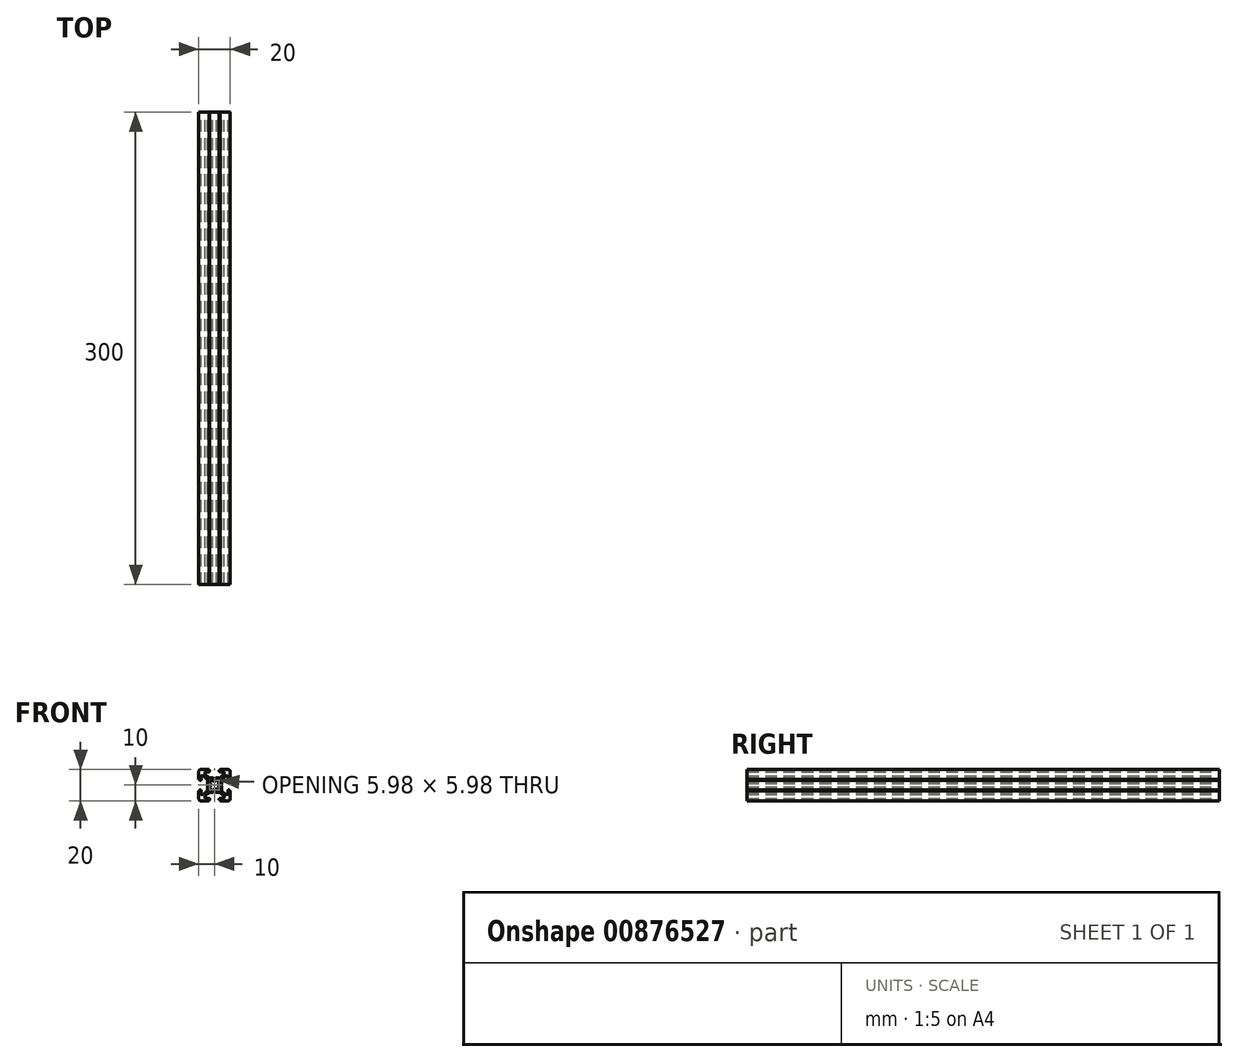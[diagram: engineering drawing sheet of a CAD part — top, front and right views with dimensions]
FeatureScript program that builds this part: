
annotation { "Feature Type Name" : "Feature", "Feature Type Description" : "" }
export const myFeature = defineFeature(function(context is Context, id is Id, definition is map)
    precondition{}
    {
        {
            var Q0;
            Q0=qCreatedBy(makeId("Front.planeOp"),FACE);
            var sketch = newSketch(context, id + "F0", { "sketchPlane" : qUnion([Q0])});
            skLineSegment(sketch, "E0", {"start": v(-222.37, -217.47) * mm, "end": v(-221.83, -218.12) * mm});
            skArc(sketch, "E1", {"start": v(-221.83, -218.12) * mm, "mid": v(-222.13, -219.38) * mm, "end": v(-221.83, -220.64) * mm});
            skLineSegment(sketch, "E2", {"start": v(-221.83, -220.64) * mm, "end": v(-222.37, -221.29) * mm});
            skArc(sketch, "E3", {"start": v(-222.37, -221.29) * mm, "mid": v(-221.9, -221.89) * mm, "end": v(-221.3, -222.37) * mm});
            skLineSegment(sketch, "E4", {"start": v(-221.3, -222.37) * mm, "end": v(-220.64, -221.83) * mm});
            skArc(sketch, "E5", {"start": v(-220.64, -221.83) * mm, "mid": v(-219.38, -222.13) * mm, "end": v(-218.12, -221.83) * mm});
            skLineSegment(sketch, "E6", {"start": v(-218.12, -221.83) * mm, "end": v(-217.47, -222.37) * mm});
            skArc(sketch, "E7", {"start": v(-217.47, -222.37) * mm, "mid": v(-216.87, -221.89) * mm, "end": v(-216.39, -221.29) * mm});
            skLineSegment(sketch, "E8", {"start": v(-216.39, -221.29) * mm, "end": v(-216.93, -220.64) * mm});
            skArc(sketch, "E9", {"start": v(-216.93, -220.64) * mm, "mid": v(-216.63, -219.38) * mm, "end": v(-216.93, -218.12) * mm});
            skLineSegment(sketch, "E10", {"start": v(-216.93, -218.12) * mm, "end": v(-216.39, -217.47) * mm});
            skArc(sketch, "E11", {"start": v(-216.39, -217.47) * mm, "mid": v(-216.87, -216.87) * mm, "end": v(-217.47, -216.4) * mm});
            skLineSegment(sketch, "E12", {"start": v(-217.47, -216.4) * mm, "end": v(-218.12, -216.93) * mm});
            skArc(sketch, "E13", {"start": v(-218.12, -216.93) * mm, "mid": v(-219.38, -216.63) * mm, "end": v(-220.64, -216.93) * mm});
            skLineSegment(sketch, "E14", {"start": v(-220.64, -216.93) * mm, "end": v(-221.3, -216.4) * mm});
            skArc(sketch, "E15", {"start": v(-221.3, -216.4) * mm, "mid": v(-221.9, -216.87) * mm, "end": v(-222.37, -217.47) * mm});
            skLineSegment(sketch, "E16", {"start": v(-223.13, -209.38) * mm, "end": v(-227.88, -209.38) * mm});
            skArc(sketch, "E17", {"start": v(-222.93, -209.58) * mm, "mid": v(-222.99, -209.44) * mm, "end": v(-223.13, -209.38) * mm});
            skLineSegment(sketch, "E18", {"start": v(-222.93, -209.68) * mm, "end": v(-222.93, -209.58) * mm});
            skArc(sketch, "E19", {"start": v(-222.93, -209.68) * mm, "mid": v(-222.87, -209.82) * mm, "end": v(-222.73, -209.88) * mm});
            skLineSegment(sketch, "E20", {"start": v(-222.58, -209.88) * mm, "end": v(-222.73, -209.88) * mm});
            skArc(sketch, "E21", {"start": v(-222.38, -210.08) * mm, "mid": v(-222.44, -209.94) * mm, "end": v(-222.58, -209.88) * mm});
            skLineSegment(sketch, "E22", {"start": v(-222.38, -210.38) * mm, "end": v(-222.38, -210.08) * mm});
            skArc(sketch, "E23", {"start": v(-222.88, -210.88) * mm, "mid": v(-222.53, -210.73) * mm, "end": v(-222.38, -210.38) * mm});
            skLineSegment(sketch, "E24", {"start": v(-224.88, -210.88) * mm, "end": v(-222.88, -210.88) * mm});
            skArc(sketch, "E25", {"start": v(-224.88, -210.88) * mm, "mid": v(-225.23, -211.03) * mm, "end": v(-225.38, -211.38) * mm});
            skLineSegment(sketch, "E26", {"start": v(-225.38, -212.11) * mm, "end": v(-225.38, -211.38) * mm});
            skArc(sketch, "E27", {"start": v(-225.38, -212.11) * mm, "mid": v(-225.34, -212.3) * mm, "end": v(-225.23, -212.47) * mm});
            skLineSegment(sketch, "E28", {"start": v(-222.97, -214.73) * mm, "end": v(-225.23, -212.47) * mm});
            skArc(sketch, "E29", {"start": v(-222.97, -214.73) * mm, "mid": v(-222.8, -214.84) * mm, "end": v(-222.61, -214.88) * mm});
            skLineSegment(sketch, "E30", {"start": v(-220.33, -214.88) * mm, "end": v(-222.61, -214.88) * mm});
            skArc(sketch, "E31", {"start": v(-220.23, -214.9) * mm, "mid": v(-220.28, -214.89) * mm, "end": v(-220.33, -214.88) * mm});
            skLineSegment(sketch, "E32", {"start": v(-219.48, -215.34) * mm, "end": v(-220.23, -214.9) * mm});
            skArc(sketch, "E33", {"start": v(-219.48, -215.34) * mm, "mid": v(-219.38, -215.37) * mm, "end": v(-219.28, -215.34) * mm});
            skLineSegment(sketch, "E34", {"start": v(-218.53, -214.9) * mm, "end": v(-219.28, -215.34) * mm});
            skArc(sketch, "E35", {"start": v(-218.43, -214.88) * mm, "mid": v(-218.48, -214.89) * mm, "end": v(-218.53, -214.9) * mm});
            skLineSegment(sketch, "E36", {"start": v(-216.15, -214.88) * mm, "end": v(-218.43, -214.88) * mm});
            skArc(sketch, "E37", {"start": v(-216.15, -214.88) * mm, "mid": v(-215.96, -214.84) * mm, "end": v(-215.8, -214.73) * mm});
            skLineSegment(sketch, "E38", {"start": v(-213.53, -212.47) * mm, "end": v(-215.8, -214.73) * mm});
            skArc(sketch, "E39", {"start": v(-213.53, -212.47) * mm, "mid": v(-213.42, -212.3) * mm, "end": v(-213.38, -212.11) * mm});
            skLineSegment(sketch, "E40", {"start": v(-213.38, -211.38) * mm, "end": v(-213.38, -212.11) * mm});
            skArc(sketch, "E41", {"start": v(-213.38, -211.38) * mm, "mid": v(-213.53, -211.03) * mm, "end": v(-213.88, -210.88) * mm});
            skLineSegment(sketch, "E42", {"start": v(-215.88, -210.88) * mm, "end": v(-213.88, -210.88) * mm});
            skArc(sketch, "E43", {"start": v(-216.38, -210.38) * mm, "mid": v(-216.23, -210.73) * mm, "end": v(-215.88, -210.88) * mm});
            skLineSegment(sketch, "E44", {"start": v(-216.38, -210.08) * mm, "end": v(-216.38, -210.38) * mm});
            skArc(sketch, "E45", {"start": v(-216.18, -209.88) * mm, "mid": v(-216.32, -209.94) * mm, "end": v(-216.38, -210.08) * mm});
            skLineSegment(sketch, "E46", {"start": v(-216.03, -209.88) * mm, "end": v(-216.18, -209.88) * mm});
            skArc(sketch, "E47", {"start": v(-216.03, -209.88) * mm, "mid": v(-215.89, -209.82) * mm, "end": v(-215.83, -209.68) * mm});
            skLineSegment(sketch, "E48", {"start": v(-215.83, -209.58) * mm, "end": v(-215.83, -209.68) * mm});
            skArc(sketch, "E49", {"start": v(-215.63, -209.38) * mm, "mid": v(-215.77, -209.44) * mm, "end": v(-215.83, -209.58) * mm});
            skLineSegment(sketch, "E50", {"start": v(-210.88, -209.38) * mm, "end": v(-215.63, -209.38) * mm});
            skArc(sketch, "E51", {"start": v(-209.38, -210.88) * mm, "mid": v(-209.82, -209.82) * mm, "end": v(-210.88, -209.38) * mm});
            skLineSegment(sketch, "E52", {"start": v(-209.38, -215.63) * mm, "end": v(-209.38, -210.88) * mm});
            skArc(sketch, "E53", {"start": v(-209.58, -215.83) * mm, "mid": v(-209.44, -215.77) * mm, "end": v(-209.38, -215.63) * mm});
            skLineSegment(sketch, "E54", {"start": v(-209.68, -215.83) * mm, "end": v(-209.58, -215.83) * mm});
            skArc(sketch, "E55", {"start": v(-209.68, -215.83) * mm, "mid": v(-209.82, -215.89) * mm, "end": v(-209.88, -216.03) * mm});
            skLineSegment(sketch, "E56", {"start": v(-209.88, -216.18) * mm, "end": v(-209.88, -216.03) * mm});
            skArc(sketch, "E57", {"start": v(-210.08, -216.38) * mm, "mid": v(-209.94, -216.32) * mm, "end": v(-209.88, -216.18) * mm});
            skLineSegment(sketch, "E58", {"start": v(-210.38, -216.38) * mm, "end": v(-210.08, -216.38) * mm});
            skArc(sketch, "E59", {"start": v(-210.88, -215.88) * mm, "mid": v(-210.73, -216.23) * mm, "end": v(-210.38, -216.38) * mm});
            skLineSegment(sketch, "E60", {"start": v(-210.88, -213.88) * mm, "end": v(-210.88, -215.88) * mm});
            skArc(sketch, "E61", {"start": v(-210.88, -213.88) * mm, "mid": v(-211.03, -213.53) * mm, "end": v(-211.38, -213.38) * mm});
            skLineSegment(sketch, "E62", {"start": v(-212.11, -213.38) * mm, "end": v(-211.38, -213.38) * mm});
            skArc(sketch, "E63", {"start": v(-212.11, -213.38) * mm, "mid": v(-212.3, -213.42) * mm, "end": v(-212.47, -213.53) * mm});
            skLineSegment(sketch, "E64", {"start": v(-214.73, -215.8) * mm, "end": v(-212.47, -213.53) * mm});
            skArc(sketch, "E65", {"start": v(-214.73, -215.8) * mm, "mid": v(-214.84, -215.96) * mm, "end": v(-214.88, -216.15) * mm});
            skLineSegment(sketch, "E66", {"start": v(-214.88, -218.43) * mm, "end": v(-214.88, -216.15) * mm});
            skArc(sketch, "E67", {"start": v(-214.9, -218.53) * mm, "mid": v(-214.89, -218.48) * mm, "end": v(-214.88, -218.43) * mm});
            skLineSegment(sketch, "E68", {"start": v(-215.34, -219.28) * mm, "end": v(-214.9, -218.53) * mm});
            skArc(sketch, "E69", {"start": v(-215.34, -219.28) * mm, "mid": v(-215.37, -219.38) * mm, "end": v(-215.34, -219.48) * mm});
            skLineSegment(sketch, "E70", {"start": v(-214.9, -220.23) * mm, "end": v(-215.34, -219.48) * mm});
            skArc(sketch, "E71", {"start": v(-214.88, -220.33) * mm, "mid": v(-214.89, -220.28) * mm, "end": v(-214.9, -220.23) * mm});
            skLineSegment(sketch, "E72", {"start": v(-214.88, -222.61) * mm, "end": v(-214.88, -220.33) * mm});
            skArc(sketch, "E73", {"start": v(-214.88, -222.61) * mm, "mid": v(-214.84, -222.8) * mm, "end": v(-214.73, -222.97) * mm});
            skLineSegment(sketch, "E74", {"start": v(-212.47, -225.23) * mm, "end": v(-214.73, -222.97) * mm});
            skArc(sketch, "E75", {"start": v(-212.47, -225.23) * mm, "mid": v(-212.3, -225.34) * mm, "end": v(-212.11, -225.38) * mm});
            skLineSegment(sketch, "E76", {"start": v(-211.38, -225.38) * mm, "end": v(-212.11, -225.38) * mm});
            skArc(sketch, "E77", {"start": v(-211.38, -225.38) * mm, "mid": v(-211.03, -225.23) * mm, "end": v(-210.88, -224.88) * mm});
            skLineSegment(sketch, "E78", {"start": v(-210.88, -222.88) * mm, "end": v(-210.88, -224.88) * mm});
            skArc(sketch, "E79", {"start": v(-210.38, -222.38) * mm, "mid": v(-210.73, -222.53) * mm, "end": v(-210.88, -222.88) * mm});
            skLineSegment(sketch, "E80", {"start": v(-210.08, -222.38) * mm, "end": v(-210.38, -222.38) * mm});
            skArc(sketch, "E81", {"start": v(-209.88, -222.58) * mm, "mid": v(-209.94, -222.44) * mm, "end": v(-210.08, -222.38) * mm});
            skLineSegment(sketch, "E82", {"start": v(-209.88, -222.73) * mm, "end": v(-209.88, -222.58) * mm});
            skArc(sketch, "E83", {"start": v(-209.88, -222.73) * mm, "mid": v(-209.82, -222.87) * mm, "end": v(-209.68, -222.93) * mm});
            skLineSegment(sketch, "E84", {"start": v(-209.58, -222.93) * mm, "end": v(-209.68, -222.93) * mm});
            skArc(sketch, "E85", {"start": v(-209.38, -223.13) * mm, "mid": v(-209.44, -222.99) * mm, "end": v(-209.58, -222.93) * mm});
            skLineSegment(sketch, "E86", {"start": v(-209.38, -227.88) * mm, "end": v(-209.38, -223.13) * mm});
            skArc(sketch, "E87", {"start": v(-210.88, -229.38) * mm, "mid": v(-209.82, -228.94) * mm, "end": v(-209.38, -227.88) * mm});
            skLineSegment(sketch, "E88", {"start": v(-215.63, -229.38) * mm, "end": v(-210.88, -229.38) * mm});
            skArc(sketch, "E89", {"start": v(-215.83, -229.18) * mm, "mid": v(-215.77, -229.32) * mm, "end": v(-215.63, -229.38) * mm});
            skLineSegment(sketch, "E90", {"start": v(-215.83, -229.08) * mm, "end": v(-215.83, -229.18) * mm});
            skArc(sketch, "E91", {"start": v(-215.83, -229.08) * mm, "mid": v(-215.89, -228.94) * mm, "end": v(-216.03, -228.88) * mm});
            skLineSegment(sketch, "E92", {"start": v(-216.18, -228.88) * mm, "end": v(-216.03, -228.88) * mm});
            skArc(sketch, "E93", {"start": v(-216.38, -228.68) * mm, "mid": v(-216.32, -228.82) * mm, "end": v(-216.18, -228.88) * mm});
            skLineSegment(sketch, "E94", {"start": v(-216.38, -228.38) * mm, "end": v(-216.38, -228.68) * mm});
            skArc(sketch, "E95", {"start": v(-215.88, -227.88) * mm, "mid": v(-216.23, -228.03) * mm, "end": v(-216.38, -228.38) * mm});
            skLineSegment(sketch, "E96", {"start": v(-213.88, -227.88) * mm, "end": v(-215.88, -227.88) * mm});
            skArc(sketch, "E97", {"start": v(-213.88, -227.88) * mm, "mid": v(-213.53, -227.73) * mm, "end": v(-213.38, -227.38) * mm});
            skLineSegment(sketch, "E98", {"start": v(-213.38, -226.65) * mm, "end": v(-213.38, -227.38) * mm});
            skArc(sketch, "E99", {"start": v(-213.38, -226.65) * mm, "mid": v(-213.42, -226.46) * mm, "end": v(-213.53, -226.3) * mm});
            skLineSegment(sketch, "E100", {"start": v(-215.8, -224.03) * mm, "end": v(-213.53, -226.3) * mm});
            skArc(sketch, "E101", {"start": v(-215.8, -224.03) * mm, "mid": v(-215.96, -223.92) * mm, "end": v(-216.15, -223.88) * mm});
            skLineSegment(sketch, "E102", {"start": v(-218.43, -223.88) * mm, "end": v(-216.15, -223.88) * mm});
            skArc(sketch, "E103", {"start": v(-218.53, -223.85) * mm, "mid": v(-218.48, -223.87) * mm, "end": v(-218.43, -223.88) * mm});
            skLineSegment(sketch, "E104", {"start": v(-219.28, -223.42) * mm, "end": v(-218.53, -223.85) * mm});
            skArc(sketch, "E105", {"start": v(-219.28, -223.42) * mm, "mid": v(-219.38, -223.4) * mm, "end": v(-219.48, -223.42) * mm});
            skLineSegment(sketch, "E106", {"start": v(-220.23, -223.85) * mm, "end": v(-219.48, -223.42) * mm});
            skArc(sketch, "E107", {"start": v(-220.33, -223.88) * mm, "mid": v(-220.28, -223.87) * mm, "end": v(-220.23, -223.85) * mm});
            skLineSegment(sketch, "E108", {"start": v(-222.61, -223.88) * mm, "end": v(-220.33, -223.88) * mm});
            skArc(sketch, "E109", {"start": v(-222.61, -223.88) * mm, "mid": v(-222.8, -223.92) * mm, "end": v(-222.97, -224.03) * mm});
            skLineSegment(sketch, "E110", {"start": v(-225.23, -226.3) * mm, "end": v(-222.97, -224.03) * mm});
            skArc(sketch, "E111", {"start": v(-225.23, -226.3) * mm, "mid": v(-225.34, -226.46) * mm, "end": v(-225.38, -226.65) * mm});
            skLineSegment(sketch, "E112", {"start": v(-225.38, -227.38) * mm, "end": v(-225.38, -226.65) * mm});
            skArc(sketch, "E113", {"start": v(-225.38, -227.38) * mm, "mid": v(-225.23, -227.73) * mm, "end": v(-224.88, -227.88) * mm});
            skLineSegment(sketch, "E114", {"start": v(-222.88, -227.88) * mm, "end": v(-224.88, -227.88) * mm});
            skArc(sketch, "E115", {"start": v(-222.38, -228.38) * mm, "mid": v(-222.53, -228.03) * mm, "end": v(-222.88, -227.88) * mm});
            skLineSegment(sketch, "E116", {"start": v(-222.38, -228.68) * mm, "end": v(-222.38, -228.38) * mm});
            skArc(sketch, "E117", {"start": v(-222.58, -228.88) * mm, "mid": v(-222.44, -228.82) * mm, "end": v(-222.38, -228.68) * mm});
            skLineSegment(sketch, "E118", {"start": v(-222.73, -228.88) * mm, "end": v(-222.58, -228.88) * mm});
            skArc(sketch, "E119", {"start": v(-222.73, -228.88) * mm, "mid": v(-222.87, -228.94) * mm, "end": v(-222.93, -229.08) * mm});
            skLineSegment(sketch, "E120", {"start": v(-222.93, -229.18) * mm, "end": v(-222.93, -229.08) * mm});
            skArc(sketch, "E121", {"start": v(-223.13, -229.38) * mm, "mid": v(-222.99, -229.32) * mm, "end": v(-222.93, -229.18) * mm});
            skLineSegment(sketch, "E122", {"start": v(-227.88, -229.38) * mm, "end": v(-223.13, -229.38) * mm});
            skArc(sketch, "E123", {"start": v(-229.38, -227.88) * mm, "mid": v(-228.94, -228.94) * mm, "end": v(-227.88, -229.38) * mm});
            skLineSegment(sketch, "E124", {"start": v(-229.38, -223.13) * mm, "end": v(-229.38, -227.88) * mm});
            skArc(sketch, "E125", {"start": v(-229.18, -222.93) * mm, "mid": v(-229.32, -222.99) * mm, "end": v(-229.38, -223.13) * mm});
            skLineSegment(sketch, "E126", {"start": v(-229.08, -222.93) * mm, "end": v(-229.18, -222.93) * mm});
            skArc(sketch, "E127", {"start": v(-229.08, -222.93) * mm, "mid": v(-228.94, -222.87) * mm, "end": v(-228.88, -222.73) * mm});
            skLineSegment(sketch, "E128", {"start": v(-228.88, -222.58) * mm, "end": v(-228.88, -222.73) * mm});
            skArc(sketch, "E129", {"start": v(-228.68, -222.38) * mm, "mid": v(-228.82, -222.44) * mm, "end": v(-228.88, -222.58) * mm});
            skLineSegment(sketch, "E130", {"start": v(-228.38, -222.38) * mm, "end": v(-228.68, -222.38) * mm});
            skArc(sketch, "E131", {"start": v(-227.88, -222.88) * mm, "mid": v(-228.03, -222.53) * mm, "end": v(-228.38, -222.38) * mm});
            skLineSegment(sketch, "E132", {"start": v(-227.88, -224.88) * mm, "end": v(-227.88, -222.88) * mm});
            skArc(sketch, "E133", {"start": v(-227.88, -224.88) * mm, "mid": v(-227.73, -225.23) * mm, "end": v(-227.38, -225.38) * mm});
            skLineSegment(sketch, "E134", {"start": v(-226.65, -225.38) * mm, "end": v(-227.38, -225.38) * mm});
            skArc(sketch, "E135", {"start": v(-226.65, -225.38) * mm, "mid": v(-226.46, -225.34) * mm, "end": v(-226.3, -225.23) * mm});
            skLineSegment(sketch, "E136", {"start": v(-224.03, -222.97) * mm, "end": v(-226.3, -225.23) * mm});
            skArc(sketch, "E137", {"start": v(-224.03, -222.97) * mm, "mid": v(-223.92, -222.8) * mm, "end": v(-223.88, -222.61) * mm});
            skLineSegment(sketch, "E138", {"start": v(-223.88, -220.33) * mm, "end": v(-223.88, -222.61) * mm});
            skArc(sketch, "E139", {"start": v(-223.85, -220.23) * mm, "mid": v(-223.87, -220.28) * mm, "end": v(-223.88, -220.33) * mm});
            skLineSegment(sketch, "E140", {"start": v(-223.42, -219.48) * mm, "end": v(-223.85, -220.23) * mm});
            skArc(sketch, "E141", {"start": v(-223.42, -219.48) * mm, "mid": v(-223.4, -219.38) * mm, "end": v(-223.42, -219.28) * mm});
            skLineSegment(sketch, "E142", {"start": v(-223.85, -218.53) * mm, "end": v(-223.42, -219.28) * mm});
            skArc(sketch, "E143", {"start": v(-223.88, -218.43) * mm, "mid": v(-223.87, -218.48) * mm, "end": v(-223.85, -218.53) * mm});
            skLineSegment(sketch, "E144", {"start": v(-223.88, -216.15) * mm, "end": v(-223.88, -218.43) * mm});
            skArc(sketch, "E145", {"start": v(-223.88, -216.15) * mm, "mid": v(-223.92, -215.96) * mm, "end": v(-224.03, -215.8) * mm});
            skLineSegment(sketch, "E146", {"start": v(-226.3, -213.53) * mm, "end": v(-224.03, -215.8) * mm});
            skArc(sketch, "E147", {"start": v(-226.3, -213.53) * mm, "mid": v(-226.46, -213.42) * mm, "end": v(-226.65, -213.38) * mm});
            skLineSegment(sketch, "E148", {"start": v(-227.38, -213.38) * mm, "end": v(-226.65, -213.38) * mm});
            skArc(sketch, "E149", {"start": v(-227.38, -213.38) * mm, "mid": v(-227.73, -213.53) * mm, "end": v(-227.88, -213.88) * mm});
            skLineSegment(sketch, "E150", {"start": v(-227.88, -215.88) * mm, "end": v(-227.88, -213.88) * mm});
            skArc(sketch, "E151", {"start": v(-228.38, -216.38) * mm, "mid": v(-228.03, -216.23) * mm, "end": v(-227.88, -215.88) * mm});
            skLineSegment(sketch, "E152", {"start": v(-228.68, -216.38) * mm, "end": v(-228.38, -216.38) * mm});
            skArc(sketch, "E153", {"start": v(-228.88, -216.18) * mm, "mid": v(-228.82, -216.32) * mm, "end": v(-228.68, -216.38) * mm});
            skLineSegment(sketch, "E154", {"start": v(-228.88, -216.03) * mm, "end": v(-228.88, -216.18) * mm});
            skArc(sketch, "E155", {"start": v(-228.88, -216.03) * mm, "mid": v(-228.94, -215.89) * mm, "end": v(-229.08, -215.83) * mm});
            skLineSegment(sketch, "E156", {"start": v(-229.18, -215.83) * mm, "end": v(-229.08, -215.83) * mm});
            skArc(sketch, "E157", {"start": v(-229.38, -215.63) * mm, "mid": v(-229.32, -215.77) * mm, "end": v(-229.18, -215.83) * mm});
            skLineSegment(sketch, "E158", {"start": v(-229.38, -210.88) * mm, "end": v(-229.38, -215.63) * mm});
            skArc(sketch, "E159", {"start": v(-227.88, -209.38) * mm, "mid": v(-228.94, -209.82) * mm, "end": v(-229.38, -210.88) * mm});
            skSolve(sketch);
        }
        {
            var Q0;
            Q0=makeQuery(id+"F0.imprint","IMPRINT",FACE,{"disambiguationData":[TD([[makeQuery(id+"F0.imprint","IMPRINT",EDGE,{"derivedFrom":sQuery(id+"F0.wireOp",EDGE,"E0")}),-1.0]])]});
            extrude(context, id + "F1", {"entities" : qUnion([Q0]), "depth" : 300 * mm, "offsetDistance" : 25 * mm});
        }
        {
            var Q0;
            Q0=makeQuery(id+"F1.opExtrude","CAP_FACE",FACE,{"disambiguationData":[OSD([sQuery(id+"F0.wireOp",EDGE,"E0"),sQuery(id+"F0.wireOp",EDGE,"E1"),sQuery(id+"F0.wireOp",EDGE,"E2"),sQuery(id+"F0.wireOp",EDGE,"E3"),sQuery(id+"F0.wireOp",EDGE,"E4"),sQuery(id+"F0.wireOp",EDGE,"E5"),sQuery(id+"F0.wireOp",EDGE,"E6"),sQuery(id+"F0.wireOp",EDGE,"E7"),sQuery(id+"F0.wireOp",EDGE,"E8"),sQuery(id+"F0.wireOp",EDGE,"E9"),sQuery(id+"F0.wireOp",EDGE,"E10"),sQuery(id+"F0.wireOp",EDGE,"E11"),sQuery(id+"F0.wireOp",EDGE,"E12"),sQuery(id+"F0.wireOp",EDGE,"E13"),sQuery(id+"F0.wireOp",EDGE,"E14"),sQuery(id+"F0.wireOp",EDGE,"E15"),sQuery(id+"F0.wireOp",EDGE,"E16"),sQuery(id+"F0.wireOp",EDGE,"E17"),sQuery(id+"F0.wireOp",EDGE,"E18"),sQuery(id+"F0.wireOp",EDGE,"E19"),sQuery(id+"F0.wireOp",EDGE,"E20"),sQuery(id+"F0.wireOp",EDGE,"E21"),sQuery(id+"F0.wireOp",EDGE,"E22"),sQuery(id+"F0.wireOp",EDGE,"E23"),sQuery(id+"F0.wireOp",EDGE,"E24"),sQuery(id+"F0.wireOp",EDGE,"E25"),sQuery(id+"F0.wireOp",EDGE,"E26"),sQuery(id+"F0.wireOp",EDGE,"E27"),sQuery(id+"F0.wireOp",EDGE,"E28"),sQuery(id+"F0.wireOp",EDGE,"E29"),sQuery(id+"F0.wireOp",EDGE,"E30"),sQuery(id+"F0.wireOp",EDGE,"E31"),sQuery(id+"F0.wireOp",EDGE,"E32"),sQuery(id+"F0.wireOp",EDGE,"E33"),sQuery(id+"F0.wireOp",EDGE,"E34"),sQuery(id+"F0.wireOp",EDGE,"E35"),sQuery(id+"F0.wireOp",EDGE,"E36"),sQuery(id+"F0.wireOp",EDGE,"E37"),sQuery(id+"F0.wireOp",EDGE,"E38"),sQuery(id+"F0.wireOp",EDGE,"E39"),sQuery(id+"F0.wireOp",EDGE,"E40"),sQuery(id+"F0.wireOp",EDGE,"E41"),sQuery(id+"F0.wireOp",EDGE,"E42"),sQuery(id+"F0.wireOp",EDGE,"E43"),sQuery(id+"F0.wireOp",EDGE,"E44"),sQuery(id+"F0.wireOp",EDGE,"E45"),sQuery(id+"F0.wireOp",EDGE,"E46"),sQuery(id+"F0.wireOp",EDGE,"E47"),sQuery(id+"F0.wireOp",EDGE,"E48"),sQuery(id+"F0.wireOp",EDGE,"E49"),sQuery(id+"F0.wireOp",EDGE,"E50"),sQuery(id+"F0.wireOp",EDGE,"E51"),sQuery(id+"F0.wireOp",EDGE,"E52"),sQuery(id+"F0.wireOp",EDGE,"E53"),sQuery(id+"F0.wireOp",EDGE,"E54"),sQuery(id+"F0.wireOp",EDGE,"E55"),sQuery(id+"F0.wireOp",EDGE,"E56"),sQuery(id+"F0.wireOp",EDGE,"E57"),sQuery(id+"F0.wireOp",EDGE,"E58"),sQuery(id+"F0.wireOp",EDGE,"E59"),sQuery(id+"F0.wireOp",EDGE,"E60"),sQuery(id+"F0.wireOp",EDGE,"E61"),sQuery(id+"F0.wireOp",EDGE,"E62"),sQuery(id+"F0.wireOp",EDGE,"E63"),sQuery(id+"F0.wireOp",EDGE,"E64"),sQuery(id+"F0.wireOp",EDGE,"E65"),sQuery(id+"F0.wireOp",EDGE,"E66"),sQuery(id+"F0.wireOp",EDGE,"E67"),sQuery(id+"F0.wireOp",EDGE,"E68"),sQuery(id+"F0.wireOp",EDGE,"E69"),sQuery(id+"F0.wireOp",EDGE,"E70"),sQuery(id+"F0.wireOp",EDGE,"E71"),sQuery(id+"F0.wireOp",EDGE,"E72"),sQuery(id+"F0.wireOp",EDGE,"E73"),sQuery(id+"F0.wireOp",EDGE,"E74"),sQuery(id+"F0.wireOp",EDGE,"E75"),sQuery(id+"F0.wireOp",EDGE,"E76"),sQuery(id+"F0.wireOp",EDGE,"E77"),sQuery(id+"F0.wireOp",EDGE,"E78"),sQuery(id+"F0.wireOp",EDGE,"E79"),sQuery(id+"F0.wireOp",EDGE,"E80"),sQuery(id+"F0.wireOp",EDGE,"E81"),sQuery(id+"F0.wireOp",EDGE,"E82"),sQuery(id+"F0.wireOp",EDGE,"E83"),sQuery(id+"F0.wireOp",EDGE,"E84"),sQuery(id+"F0.wireOp",EDGE,"E85"),sQuery(id+"F0.wireOp",EDGE,"E86"),sQuery(id+"F0.wireOp",EDGE,"E87"),sQuery(id+"F0.wireOp",EDGE,"E88"),sQuery(id+"F0.wireOp",EDGE,"E89"),sQuery(id+"F0.wireOp",EDGE,"E90"),sQuery(id+"F0.wireOp",EDGE,"E91"),sQuery(id+"F0.wireOp",EDGE,"E92"),sQuery(id+"F0.wireOp",EDGE,"E93"),sQuery(id+"F0.wireOp",EDGE,"E94"),sQuery(id+"F0.wireOp",EDGE,"E95"),sQuery(id+"F0.wireOp",EDGE,"E96"),sQuery(id+"F0.wireOp",EDGE,"E97"),sQuery(id+"F0.wireOp",EDGE,"E98"),sQuery(id+"F0.wireOp",EDGE,"E99"),sQuery(id+"F0.wireOp",EDGE,"E100"),sQuery(id+"F0.wireOp",EDGE,"E101"),sQuery(id+"F0.wireOp",EDGE,"E102"),sQuery(id+"F0.wireOp",EDGE,"E103"),sQuery(id+"F0.wireOp",EDGE,"E104"),sQuery(id+"F0.wireOp",EDGE,"E105"),sQuery(id+"F0.wireOp",EDGE,"E106"),sQuery(id+"F0.wireOp",EDGE,"E107"),sQuery(id+"F0.wireOp",EDGE,"E108"),sQuery(id+"F0.wireOp",EDGE,"E109"),sQuery(id+"F0.wireOp",EDGE,"E110"),sQuery(id+"F0.wireOp",EDGE,"E111"),sQuery(id+"F0.wireOp",EDGE,"E112"),sQuery(id+"F0.wireOp",EDGE,"E113"),sQuery(id+"F0.wireOp",EDGE,"E114"),sQuery(id+"F0.wireOp",EDGE,"E115"),sQuery(id+"F0.wireOp",EDGE,"E116"),sQuery(id+"F0.wireOp",EDGE,"E117"),sQuery(id+"F0.wireOp",EDGE,"E118"),sQuery(id+"F0.wireOp",EDGE,"E119"),sQuery(id+"F0.wireOp",EDGE,"E120"),sQuery(id+"F0.wireOp",EDGE,"E121"),sQuery(id+"F0.wireOp",EDGE,"E122"),sQuery(id+"F0.wireOp",EDGE,"E123"),sQuery(id+"F0.wireOp",EDGE,"E124"),sQuery(id+"F0.wireOp",EDGE,"E125"),sQuery(id+"F0.wireOp",EDGE,"E126"),sQuery(id+"F0.wireOp",EDGE,"E127"),sQuery(id+"F0.wireOp",EDGE,"E128"),sQuery(id+"F0.wireOp",EDGE,"E129"),sQuery(id+"F0.wireOp",EDGE,"E130"),sQuery(id+"F0.wireOp",EDGE,"E131"),sQuery(id+"F0.wireOp",EDGE,"E132"),sQuery(id+"F0.wireOp",EDGE,"E133"),sQuery(id+"F0.wireOp",EDGE,"E134"),sQuery(id+"F0.wireOp",EDGE,"E135"),sQuery(id+"F0.wireOp",EDGE,"E136"),sQuery(id+"F0.wireOp",EDGE,"E137"),sQuery(id+"F0.wireOp",EDGE,"E138"),sQuery(id+"F0.wireOp",EDGE,"E139"),sQuery(id+"F0.wireOp",EDGE,"E140"),sQuery(id+"F0.wireOp",EDGE,"E141"),sQuery(id+"F0.wireOp",EDGE,"E142"),sQuery(id+"F0.wireOp",EDGE,"E143"),sQuery(id+"F0.wireOp",EDGE,"E144"),sQuery(id+"F0.wireOp",EDGE,"E145"),sQuery(id+"F0.wireOp",EDGE,"E146"),sQuery(id+"F0.wireOp",EDGE,"E147"),sQuery(id+"F0.wireOp",EDGE,"E148"),sQuery(id+"F0.wireOp",EDGE,"E149"),sQuery(id+"F0.wireOp",EDGE,"E150"),sQuery(id+"F0.wireOp",EDGE,"E151"),sQuery(id+"F0.wireOp",EDGE,"E152"),sQuery(id+"F0.wireOp",EDGE,"E153"),sQuery(id+"F0.wireOp",EDGE,"E154"),sQuery(id+"F0.wireOp",EDGE,"E155"),sQuery(id+"F0.wireOp",EDGE,"E156"),sQuery(id+"F0.wireOp",EDGE,"E157"),sQuery(id+"F0.wireOp",EDGE,"E158"),sQuery(id+"F0.wireOp",EDGE,"E159")])],"isStart":true});
            var sketch = newSketch(context, id + "F2", { "sketchPlane" : qUnion([Q0])});
            skLineSegment(sketch, "E160", {"start": v(216.93, -218.12) * mm, "end": v(221.83, -220.64) * mm, "construction": true});
            skLineSegment(sketch, "E161", {"start": v(221.83, -220.64) * mm, "end": v(218.12, -221.83) * mm, "construction": true});
            skLineSegment(sketch, "E162", {"start": v(218.12, -221.83) * mm, "end": v(220.64, -216.93) * mm, "construction": true});
            skLineSegment(sketch, "E163", {"start": v(220.64, -216.93) * mm, "end": v(216.93, -218.12) * mm, "construction": true});
            skPoint(sketch, "E164", {"position": v(219.38, -219.38) * mm});
            skLineSegment(sketch, "E165", {"start": v(219.38, -219.38) * mm, "end": v(0, 0) * mm});
            skSolve(sketch);
        }
        {
            var Q0;
            Q0=makeQuery(id+"F1.opExtrude","SWEPT_BODY",BODY,{"disambiguationData":[OSD([sQuery(id+"F0.wireOp",EDGE,"E0"),sQuery(id+"F0.wireOp",EDGE,"E1"),sQuery(id+"F0.wireOp",EDGE,"E2"),sQuery(id+"F0.wireOp",EDGE,"E3"),sQuery(id+"F0.wireOp",EDGE,"E4"),sQuery(id+"F0.wireOp",EDGE,"E5"),sQuery(id+"F0.wireOp",EDGE,"E6"),sQuery(id+"F0.wireOp",EDGE,"E7"),sQuery(id+"F0.wireOp",EDGE,"E8"),sQuery(id+"F0.wireOp",EDGE,"E9"),sQuery(id+"F0.wireOp",EDGE,"E10"),sQuery(id+"F0.wireOp",EDGE,"E11"),sQuery(id+"F0.wireOp",EDGE,"E12"),sQuery(id+"F0.wireOp",EDGE,"E13"),sQuery(id+"F0.wireOp",EDGE,"E14"),sQuery(id+"F0.wireOp",EDGE,"E15"),sQuery(id+"F0.wireOp",EDGE,"E16"),sQuery(id+"F0.wireOp",EDGE,"E17"),sQuery(id+"F0.wireOp",EDGE,"E18"),sQuery(id+"F0.wireOp",EDGE,"E19"),sQuery(id+"F0.wireOp",EDGE,"E20"),sQuery(id+"F0.wireOp",EDGE,"E21"),sQuery(id+"F0.wireOp",EDGE,"E22"),sQuery(id+"F0.wireOp",EDGE,"E23"),sQuery(id+"F0.wireOp",EDGE,"E24"),sQuery(id+"F0.wireOp",EDGE,"E25"),sQuery(id+"F0.wireOp",EDGE,"E26"),sQuery(id+"F0.wireOp",EDGE,"E27"),sQuery(id+"F0.wireOp",EDGE,"E28"),sQuery(id+"F0.wireOp",EDGE,"E29"),sQuery(id+"F0.wireOp",EDGE,"E30"),sQuery(id+"F0.wireOp",EDGE,"E31"),sQuery(id+"F0.wireOp",EDGE,"E32"),sQuery(id+"F0.wireOp",EDGE,"E33"),sQuery(id+"F0.wireOp",EDGE,"E34"),sQuery(id+"F0.wireOp",EDGE,"E35"),sQuery(id+"F0.wireOp",EDGE,"E36"),sQuery(id+"F0.wireOp",EDGE,"E37"),sQuery(id+"F0.wireOp",EDGE,"E38"),sQuery(id+"F0.wireOp",EDGE,"E39"),sQuery(id+"F0.wireOp",EDGE,"E40"),sQuery(id+"F0.wireOp",EDGE,"E41"),sQuery(id+"F0.wireOp",EDGE,"E42"),sQuery(id+"F0.wireOp",EDGE,"E43"),sQuery(id+"F0.wireOp",EDGE,"E44"),sQuery(id+"F0.wireOp",EDGE,"E45"),sQuery(id+"F0.wireOp",EDGE,"E46"),sQuery(id+"F0.wireOp",EDGE,"E47"),sQuery(id+"F0.wireOp",EDGE,"E48"),sQuery(id+"F0.wireOp",EDGE,"E49"),sQuery(id+"F0.wireOp",EDGE,"E50"),sQuery(id+"F0.wireOp",EDGE,"E51"),sQuery(id+"F0.wireOp",EDGE,"E52"),sQuery(id+"F0.wireOp",EDGE,"E53"),sQuery(id+"F0.wireOp",EDGE,"E54"),sQuery(id+"F0.wireOp",EDGE,"E55"),sQuery(id+"F0.wireOp",EDGE,"E56"),sQuery(id+"F0.wireOp",EDGE,"E57"),sQuery(id+"F0.wireOp",EDGE,"E58"),sQuery(id+"F0.wireOp",EDGE,"E59"),sQuery(id+"F0.wireOp",EDGE,"E60"),sQuery(id+"F0.wireOp",EDGE,"E61"),sQuery(id+"F0.wireOp",EDGE,"E62"),sQuery(id+"F0.wireOp",EDGE,"E63"),sQuery(id+"F0.wireOp",EDGE,"E64"),sQuery(id+"F0.wireOp",EDGE,"E65"),sQuery(id+"F0.wireOp",EDGE,"E66"),sQuery(id+"F0.wireOp",EDGE,"E67"),sQuery(id+"F0.wireOp",EDGE,"E68"),sQuery(id+"F0.wireOp",EDGE,"E69"),sQuery(id+"F0.wireOp",EDGE,"E70"),sQuery(id+"F0.wireOp",EDGE,"E71"),sQuery(id+"F0.wireOp",EDGE,"E72"),sQuery(id+"F0.wireOp",EDGE,"E73"),sQuery(id+"F0.wireOp",EDGE,"E74"),sQuery(id+"F0.wireOp",EDGE,"E75"),sQuery(id+"F0.wireOp",EDGE,"E76"),sQuery(id+"F0.wireOp",EDGE,"E77"),sQuery(id+"F0.wireOp",EDGE,"E78"),sQuery(id+"F0.wireOp",EDGE,"E79"),sQuery(id+"F0.wireOp",EDGE,"E80"),sQuery(id+"F0.wireOp",EDGE,"E81"),sQuery(id+"F0.wireOp",EDGE,"E82"),sQuery(id+"F0.wireOp",EDGE,"E83"),sQuery(id+"F0.wireOp",EDGE,"E84"),sQuery(id+"F0.wireOp",EDGE,"E85"),sQuery(id+"F0.wireOp",EDGE,"E86"),sQuery(id+"F0.wireOp",EDGE,"E87"),sQuery(id+"F0.wireOp",EDGE,"E88"),sQuery(id+"F0.wireOp",EDGE,"E89"),sQuery(id+"F0.wireOp",EDGE,"E90"),sQuery(id+"F0.wireOp",EDGE,"E91"),sQuery(id+"F0.wireOp",EDGE,"E92"),sQuery(id+"F0.wireOp",EDGE,"E93"),sQuery(id+"F0.wireOp",EDGE,"E94"),sQuery(id+"F0.wireOp",EDGE,"E95"),sQuery(id+"F0.wireOp",EDGE,"E96"),sQuery(id+"F0.wireOp",EDGE,"E97"),sQuery(id+"F0.wireOp",EDGE,"E98"),sQuery(id+"F0.wireOp",EDGE,"E99"),sQuery(id+"F0.wireOp",EDGE,"E100"),sQuery(id+"F0.wireOp",EDGE,"E101"),sQuery(id+"F0.wireOp",EDGE,"E102"),sQuery(id+"F0.wireOp",EDGE,"E103"),sQuery(id+"F0.wireOp",EDGE,"E104"),sQuery(id+"F0.wireOp",EDGE,"E105"),sQuery(id+"F0.wireOp",EDGE,"E106"),sQuery(id+"F0.wireOp",EDGE,"E107"),sQuery(id+"F0.wireOp",EDGE,"E108"),sQuery(id+"F0.wireOp",EDGE,"E109"),sQuery(id+"F0.wireOp",EDGE,"E110"),sQuery(id+"F0.wireOp",EDGE,"E111"),sQuery(id+"F0.wireOp",EDGE,"E112"),sQuery(id+"F0.wireOp",EDGE,"E113"),sQuery(id+"F0.wireOp",EDGE,"E114"),sQuery(id+"F0.wireOp",EDGE,"E115"),sQuery(id+"F0.wireOp",EDGE,"E116"),sQuery(id+"F0.wireOp",EDGE,"E117"),sQuery(id+"F0.wireOp",EDGE,"E118"),sQuery(id+"F0.wireOp",EDGE,"E119"),sQuery(id+"F0.wireOp",EDGE,"E120"),sQuery(id+"F0.wireOp",EDGE,"E121"),sQuery(id+"F0.wireOp",EDGE,"E122"),sQuery(id+"F0.wireOp",EDGE,"E123"),sQuery(id+"F0.wireOp",EDGE,"E124"),sQuery(id+"F0.wireOp",EDGE,"E125"),sQuery(id+"F0.wireOp",EDGE,"E126"),sQuery(id+"F0.wireOp",EDGE,"E127"),sQuery(id+"F0.wireOp",EDGE,"E128"),sQuery(id+"F0.wireOp",EDGE,"E129"),sQuery(id+"F0.wireOp",EDGE,"E130"),sQuery(id+"F0.wireOp",EDGE,"E131"),sQuery(id+"F0.wireOp",EDGE,"E132"),sQuery(id+"F0.wireOp",EDGE,"E133"),sQuery(id+"F0.wireOp",EDGE,"E134"),sQuery(id+"F0.wireOp",EDGE,"E135"),sQuery(id+"F0.wireOp",EDGE,"E136"),sQuery(id+"F0.wireOp",EDGE,"E137"),sQuery(id+"F0.wireOp",EDGE,"E138"),sQuery(id+"F0.wireOp",EDGE,"E139"),sQuery(id+"F0.wireOp",EDGE,"E140"),sQuery(id+"F0.wireOp",EDGE,"E141"),sQuery(id+"F0.wireOp",EDGE,"E142"),sQuery(id+"F0.wireOp",EDGE,"E143"),sQuery(id+"F0.wireOp",EDGE,"E144"),sQuery(id+"F0.wireOp",EDGE,"E145"),sQuery(id+"F0.wireOp",EDGE,"E146"),sQuery(id+"F0.wireOp",EDGE,"E147"),sQuery(id+"F0.wireOp",EDGE,"E148"),sQuery(id+"F0.wireOp",EDGE,"E149"),sQuery(id+"F0.wireOp",EDGE,"E150"),sQuery(id+"F0.wireOp",EDGE,"E151"),sQuery(id+"F0.wireOp",EDGE,"E152"),sQuery(id+"F0.wireOp",EDGE,"E153"),sQuery(id+"F0.wireOp",EDGE,"E154"),sQuery(id+"F0.wireOp",EDGE,"E155"),sQuery(id+"F0.wireOp",EDGE,"E156"),sQuery(id+"F0.wireOp",EDGE,"E157"),sQuery(id+"F0.wireOp",EDGE,"E158"),sQuery(id+"F0.wireOp",EDGE,"E159")])]});
            var Q1;
            Q1=sQuery(id+"F2.wireOp",EDGE,"E165");
            transform(context, id + "F3", {"entities" : qUnion([Q0]), "transformType" : TransformType.TRANSLATION_ENTITY, "oppositeDirectionEntity" : false, "transformLine" : qUnion([Q1]), "makeCopy" : false});
        }
    });
